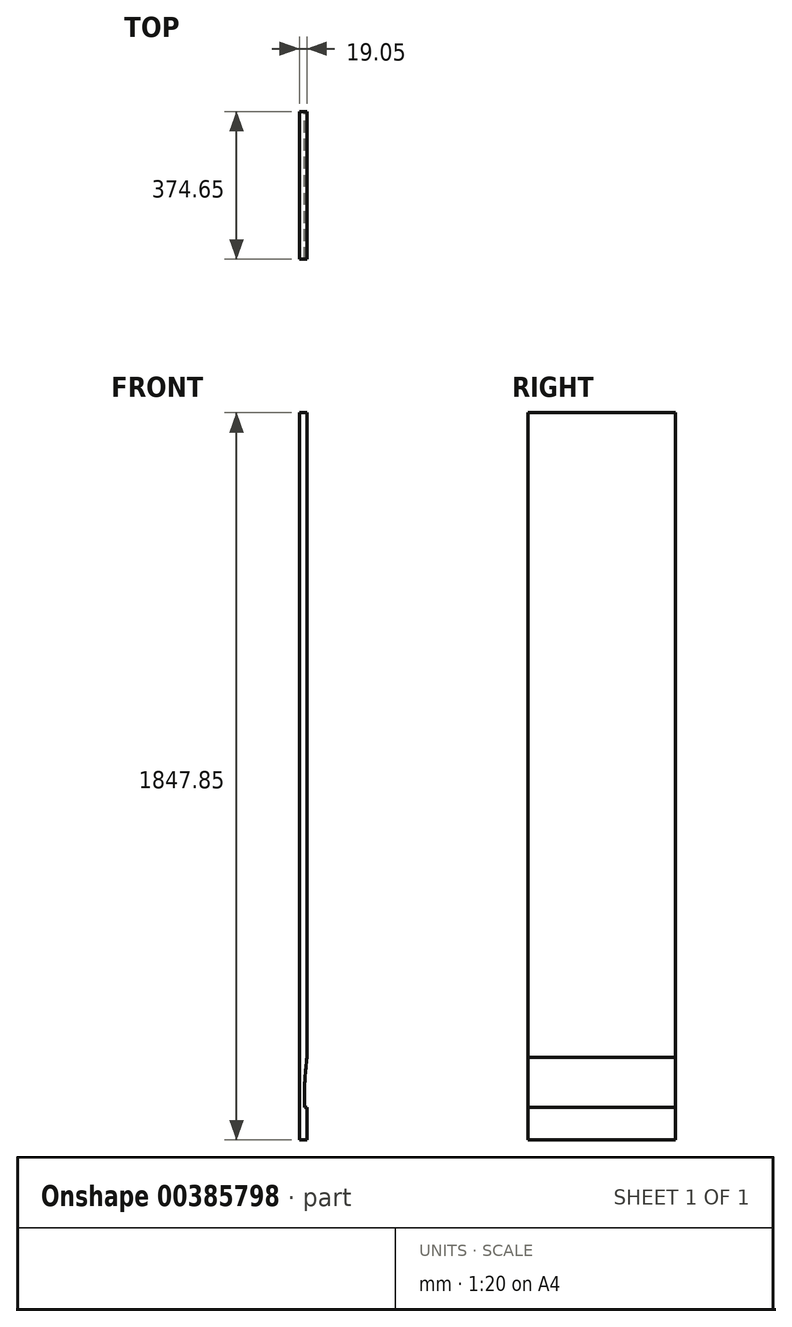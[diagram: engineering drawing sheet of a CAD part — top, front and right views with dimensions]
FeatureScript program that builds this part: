
annotation { "Feature Type Name" : "Feature", "Feature Type Description" : "" }
export const myFeature = defineFeature(function(context is Context, id is Id, definition is map)
    precondition{}
    {
        {
            var Q0;
            Q0=qCreatedBy(makeId("Front.planeOp"),FACE);
            var sketch = newSketch(context, id + "F0", { "sketchPlane" : qUnion([Q0])});
            skLineSegment(sketch, "E0.bottom", {"start": v(0, 0) * mm, "end": v(-19.05, 0) * mm});
            skLineSegment(sketch, "E0.top", {"start": v(0, 1847.85) * mm, "end": v(-19.05, 1847.85) * mm});
            skLineSegment(sketch, "E0.left", {"start": v(0, 0) * mm, "end": v(0, 1847.85) * mm});
            skLineSegment(sketch, "E0.right", {"start": v(-19.05, 0) * mm, "end": v(-19.05, 1847.85) * mm});
            skSolve(sketch);
        }
        {
            var Q0;
            Q0=makeQuery(id+"F0.imprint","IMPRINT",FACE,{"disambiguationData":[TD([[makeQuery(id+"F0.imprint","IMPRINT",EDGE,{"derivedFrom":sQuery(id+"F0.wireOp",EDGE,"E0.bottom")}),-1.0]])]});
            extrude(context, id + "F1", {"entities" : qUnion([Q0]), "depth" : 374.65 * mm});
        }
        {
            var Q0;
            Q0=makeQuery(id+"F1.opExtrude","CAP_FACE",FACE,{"disambiguationData":[OSD([sQuery(id+"F0.wireOp",EDGE,"E0.bottom"),sQuery(id+"F0.wireOp",EDGE,"E0.top"),sQuery(id+"F0.wireOp",EDGE,"E0.left"),sQuery(id+"F0.wireOp",EDGE,"E0.right")])],"isStart":true});
            var sketch = newSketch(context, id + "F2", { "sketchPlane" : qUnion([Q0])});
            skLineSegment(sketch, "E1.0", {"start": v(0, 1701.8) * mm, "end": v(19.05, 1701.8) * mm, "construction": true});
            skLineSegment(sketch, "E2", {"start": v(0, 1054.1) * mm, "end": v(19.05, 1054.1) * mm});
            skLineSegment(sketch, "E3", {"start": v(0, 730.25) * mm, "end": v(19.05, 730.25) * mm});
            skLineSegment(sketch, "E4", {"start": v(0, 406.4) * mm, "end": v(19.05, 406.4) * mm});
            skLineSegment(sketch, "E5", {"start": v(6.35, 101.6) * mm, "end": v(19.05, 101.6) * mm});
            skLineSegment(sketch, "E6", {"start": v(0, 1377.95) * mm, "end": v(19.05, 1377.95) * mm});
            skLineSegment(sketch, "E7.0", {"start": v(6.35, 0) * mm, "end": v(6.35, 1847.85) * mm});
            skLineSegment(sketch, "E8.0", {"start": v(0, 1073.15) * mm, "end": v(19.05, 1073.15) * mm, "construction": true});
            skLineSegment(sketch, "E9.0", {"start": v(0, 1397) * mm, "end": v(19.05, 1397) * mm, "construction": true});
            skLineSegment(sketch, "E10.0", {"start": v(0, 1720.85) * mm, "end": v(19.05, 1720.85) * mm});
            skLineSegment(sketch, "E11.0", {"start": v(0, 749.3) * mm, "end": v(19.05, 749.3) * mm});
            skLineSegment(sketch, "E12.0", {"start": v(0, 425.45) * mm, "end": v(19.05, 425.45) * mm});
            skLineSegment(sketch, "E13.0", {"start": v(0, 82.55) * mm, "end": v(19.05, 82.55) * mm});
            skLineSegment(sketch, "E14", {"start": v(0, 209.79) * mm, "end": v(19.05, 209.79) * mm});
            skPoint(sketch, "E15", {"position": v(6.35, 101.6) * mm});
            skArc(sketch, "E16", {"start": v(6.35, 101.6) * mm, "mid": v(4.78, 155.79) * mm, "end": v(0, 209.79) * mm});
            skPoint(sketch, "E17.orphan", {"position": v(0, 101.6) * mm});
            skLineSegment(sketch, "E18", {"start": v(0, 82.55) * mm, "end": v(-37.04, 82.55) * mm});
            skLineSegment(sketch, "E19", {"start": v(-37.04, 82.55) * mm, "end": v(-25.77, 209.79) * mm});
            skLineSegment(sketch, "E20", {"start": v(-25.77, 209.79) * mm, "end": v(0, 209.79) * mm});
            skPoint(sketch, "E21", {"position": v(0, 533.63) * mm});
            skPoint(sketch, "E22", {"position": v(0, 857.48) * mm});
            skPoint(sketch, "E23", {"position": v(0, 1181.33) * mm});
            skPoint(sketch, "E24", {"position": v(0, 1505.18) * mm});
            skPoint(sketch, "E25", {"position": v(6.35, 425.45) * mm});
            skPoint(sketch, "E26", {"position": v(6.35, 749.3) * mm});
            skPoint(sketch, "E27", {"position": v(6.35, 1073.15) * mm});
            skPoint(sketch, "E28", {"position": v(6.35, 1397) * mm});
            skSolve(sketch);
        }
        {
            var Q0;
            {var subQ3=sQuery(id+"F2.wireOp",EDGE,"E7.0");var subQ5=sQuery(id+"F2.wireOp",EDGE,"E13.0");var subQ7=makeQuery(id+"F2.imprint","INTERSECT",VERTEX,{"derivedFrom":[subQ3,subQ5]});Q0=makeQuery(id+"F2.imprint","IMPRINT",FACE,{"disambiguationData":[TD([[makeQuery(id+"F2.imprint","IMPRINT",EDGE,{"disambiguationData":[TD([[subQ7,-1.0]])],"derivedFrom":subQ3}),1.0]])]});}
            var Q1;
            {var subQ0=sQuery(id+"F2.wireOp",EDGE,"E18");Q1=makeQuery(id+"F2.imprint","IMPRINT",FACE,{"disambiguationData":[TD([[makeQuery(id+"F2.imprint","IMPRINT",EDGE,{"derivedFrom":subQ0}),-1.0]])]});}
            extrude(context, id + "F3", {"entities" : qUnion([Q0, Q1]), "operationType" : NewBodyOperationType.REMOVE, "endBound" : BoundingType.THROUGH_ALL, "oppositeDirection" : true, "depth" : 25.4 * mm});
        }
    });
